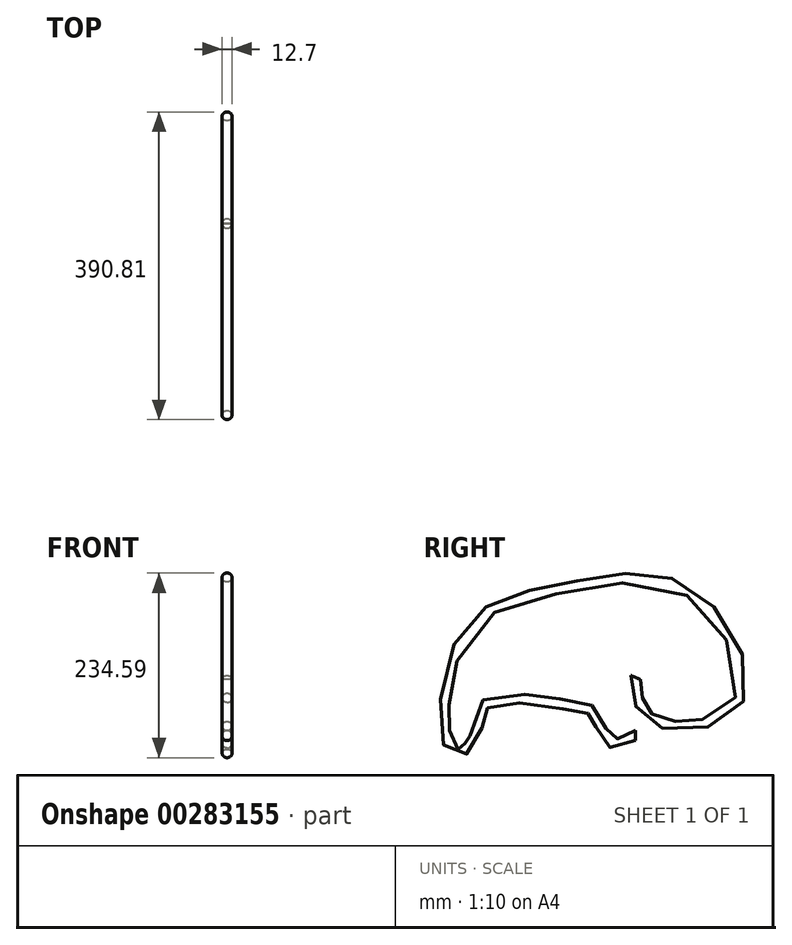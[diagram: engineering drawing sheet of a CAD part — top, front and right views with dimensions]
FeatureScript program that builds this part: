
annotation { "Feature Type Name" : "Feature", "Feature Type Description" : "" }
export const myFeature = defineFeature(function(context is Context, id is Id, definition is map)
    precondition{}
    {
        {
            var Q0;
            Q0=qCreatedBy(makeId("Right.planeOp"),FACE);
            var sketch = newSketch(context, id + "F0", { "sketchPlane" : qUnion([Q0])});
            skFitSpline(sketch, "E0", {"points": [v(0, 0) * mm, v(-35.04, -7.66) * mm, v(-49.78, 26.15) * mm, v(-74.06, 36.55) * mm, v(-187.63, 42.62) * mm, v(-204.1, 0) * mm, v(-231.85, -20.67) * mm, v(-219.71, 124.98) * mm, v(-86.2, 188.28) * mm, v(68.13, 183.07) * mm, v(129.68, 42.62) * mm, v(22.18, 20.08) * mm, v(0, 73.83) * mm], "startDerivative": vector(-734.08, -364.76) * mm, "endDerivative": vector(-53.53, 911.55) * mm});
            skSolve(sketch);
        }
        {
            var Q0;
            Q0=qCreatedBy(makeId("Front.planeOp"),FACE);
            var sketch = newSketch(context, id + "F1", { "sketchPlane" : qUnion([Q0])});
            skCircle(sketch, "E1", {"center": v(0, 0) * mm, "radius": 6.35 * mm});
            skSolve(sketch);
        }
        {
            var Q0;
            Q0=makeQuery(id+"F1.imprint","IMPRINT",FACE,{"disambiguationData":[TD([[makeQuery(id+"F1.imprint","IMPRINT",EDGE,{"derivedFrom":sQuery(id+"F1.wireOp",EDGE,"E1")}),1.0]])]});
            var Q1;
            Q1=sQuery(id+"F0.wireOp",EDGE,"E0");
            sweep(context, id + "F2", {"profiles" : qUnion([Q0]), "path" : qUnion([Q1])});
        }
    });
